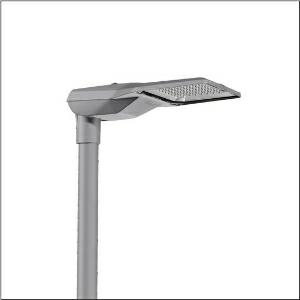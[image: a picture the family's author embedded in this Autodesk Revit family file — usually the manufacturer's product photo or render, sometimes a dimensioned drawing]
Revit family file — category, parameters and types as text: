
# Revit family: streetlight_sl_21_midi___pc-r_5xe3g33s08mb_c3de
name_source: partatom
category: Lighting Fixtures
units: mm (PartAtom-declared; Revit-internal decimal feet)

## family parameters
Cut with Voids When Loaded = No
Host = Face
Light Source = No
Part Type = Normal
Room Calculation Point = No
Round Connector Dimension = Use Diameter
Shared = No

## types (1)
- --- (1 x LED, 17390 lm, 136 W, 3000K)
    Apparent Load = 136 VA
    CIE Flux Codes = 38 78 98 100 100
    Color Rendering = 70
    Color Temperature = 3000K
    Default Elevation = 1800 mm
    Description = Streetlight SL 21 midi, mast luminaire, primary light control with lens, of PMMA, primary optical cover: cover, of toughened safety glass, transparent, light distribution: PC-R, light emission: direct distribution, primary light characteristic: asymmetric, right, installation type: side-entry, post-top, LED, High Power LED, rated luminous flux: 17.390lm, luminous efficacy: 128lm/W, light colour: 730, colour temperature: 3000K, control gear: D4i, control: overheat protection, constant luminous flux control, time-dependent luminous flux control, flexible luminous flux parameterisation, pre-setting: logarithmic dimming characteristic, mains connection: 230..240V, AC, 50/60Hz, start of lifetime: 136W, end of service life: 142W, reduction: 61W, luminaire housing, of diecast aluminium, powder-coated, Siteco® metallic grey (DB 702S), corrosivity category C5 mid according to DIN EN ISO 12944, please order mast flange separately, inclination adjustable: 0°, 5°, 10°, 15°, sealing non-destructively replaceable, multi-level sealing system, length: 644mm, width: 335mm, height: 110mm, mast flange for spigot size: 42mm (side-entry): 5XC10008XM4, 60/48mm (side-entry/post-top): 5XC10108XM2, 76/60mm (side-entry/post-top): 5XC10108XM1, mounting height: 4..8m, Smart Interface above, protection rating (complete): IP66, insulation class (complete): insulation class II (safety insulation), certification: CE, ENEC, ENEC+, VDE, impact resistance: IK10, permissible operating ambient temperature for outdoor applications: -40..+50°C, standard-compliant lighting for roads and squares, packaging unit: 1 piece

Light Distribution: PC-R
    Height = 111 mm
    Lamp = 1 x LED
    Lamp Light Flux = 17390 lm
    Lamp Power = 136 W
    Lamp count = 1
    Length = 644 mm
    Luminous efficacy = 128 lm/W
    Manufacturer = Siteco
    ModVariant = No
    Model = 5XE3G33S08MB
    Number of Poles = 1
    OnlyDefault = Yes
    Power Factor = 1
    Product Name = Streetlight SL 21 midi | PC-R
    Product group = mast luminaire | pylon top
    ProductGroupID = 6100
    Protection Class = Protection class II
    Protection Degree = IP 66
    RLX_Detail_Level = 1
    RLX_Emergency_Light_Flux = 0 lm
    RLX_Emergency_Type = 0
    RLX_Emergency_Type_DB = No
    RlxData = <blob elided: 29373 chars, md5=56f2a771>
    Socket = socket
    Standby Power = 0 W
    System Light Flux = 17390 lm
    System Power = 136 W
    Type Comments = factory setting: luminous flux: 100 % | dim-lin: 254 | 695 mA
    Type Image = l_1004302.jpg
    URL = http://relux.com
    VarID = @adj_064388
    Voltage = 0 V
    Weight = 0.00 kg
    Width = 336 mm

## geometry (parser evidence)
native form markers: Blend x4, Sweep x11
no freeform markers — native parametric forms only
